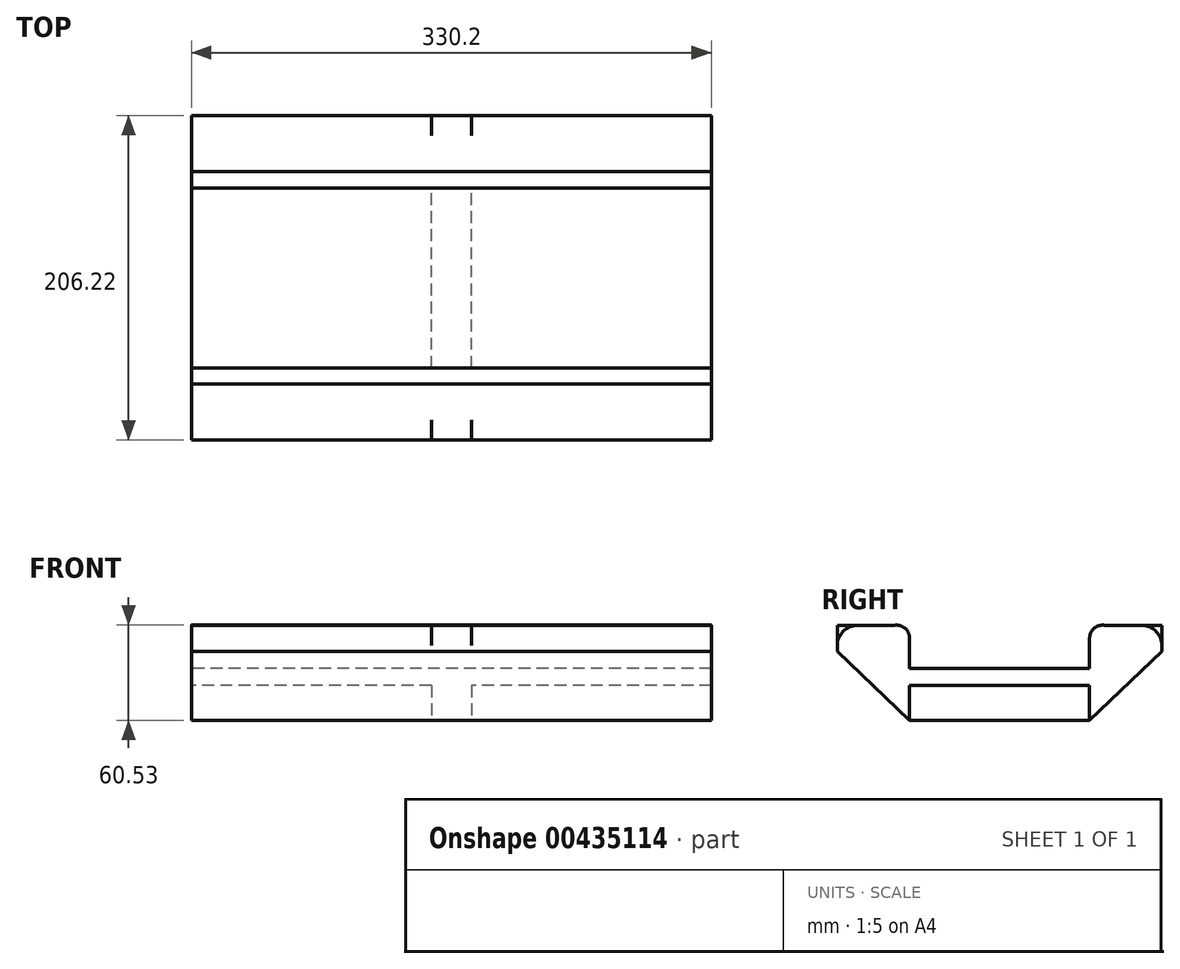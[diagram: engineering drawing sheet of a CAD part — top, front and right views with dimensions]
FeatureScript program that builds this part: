
annotation { "Feature Type Name" : "Feature", "Feature Type Description" : "" }
export const myFeature = defineFeature(function(context is Context, id is Id, definition is map)
    precondition{}
    {
        {
            var Q0;
            Q0=qCreatedBy(makeId("Right.planeOp"),FACE);
            var sketch = newSketch(context, id + "F0", { "sketchPlane" : qUnion([Q0])});
            skLineSegment(sketch, "E0.bottom", {"start": v(-57.15, 16.51) * mm, "end": v(57.15, 16.51) * mm});
            skLineSegment(sketch, "E0.top", {"start": v(-57.15, -16.51) * mm, "end": v(57.15, -16.51) * mm});
            skLineSegment(sketch, "E0.left", {"start": v(-57.15, 16.51) * mm, "end": v(-57.15, -16.51) * mm});
            skLineSegment(sketch, "E0.right", {"start": v(57.15, 16.51) * mm, "end": v(57.15, -16.51) * mm});
            skPoint(sketch, "E0.middle", {"position": v(0, 0) * mm});
            skLineSegment(sketch, "E1", {"start": v(-57.15, 16.51) * mm, "end": v(-57.15, 35.56) * mm});
            skLineSegment(sketch, "E2", {"start": v(57.15, 16.51) * mm, "end": v(57.15, 35.56) * mm});
            skLineSegment(sketch, "E3.bottom", {"start": v(-80.96, 43.82) * mm, "end": v(-103.11, 43.82) * mm});
            skLineSegment(sketch, "E3.top", {"start": v(-80.96, 27.3) * mm, "end": v(-103.11, 27.3) * mm});
            skLineSegment(sketch, "E3.left", {"start": v(-80.96, 43.82) * mm, "end": v(-80.96, 27.3) * mm});
            skLineSegment(sketch, "E3.right", {"start": v(-103.11, 43.82) * mm, "end": v(-103.11, 27.3) * mm});
            skPoint(sketch, "E3.middle", {"position": v(-92.04, 35.56) * mm});
            skLineSegment(sketch, "E4.bottom", {"start": v(103.11, 27.3) * mm, "end": v(81.47, 27.3) * mm});
            skLineSegment(sketch, "E4.top", {"start": v(103.11, 43.82) * mm, "end": v(81.47, 43.82) * mm});
            skLineSegment(sketch, "E4.left", {"start": v(103.11, 27.3) * mm, "end": v(103.11, 43.82) * mm});
            skLineSegment(sketch, "E4.right", {"start": v(81.47, 27.3) * mm, "end": v(81.47, 43.82) * mm});
            skPoint(sketch, "E4.middle", {"position": v(92.3, 35.56) * mm});
            skArc(sketch, "E5", {"start": v(-57.15, 35.56) * mm, "mid": v(-60.32, 42.16) * mm, "end": v(-67.46, 43.81) * mm});
            skArc(sketch, "E6", {"start": v(57.15, 35.56) * mm, "mid": v(60.32, 42.16) * mm, "end": v(67.46, 43.82) * mm});
            skLineSegment(sketch, "E7", {"start": v(-67.46, 43.82) * mm, "end": v(-80.96, 43.82) * mm});
            skLineSegment(sketch, "E8", {"start": v(67.46, 43.82) * mm, "end": v(81.47, 43.82) * mm});
            skLineSegment(sketch, "E9", {"start": v(-103.11, 27.3) * mm, "end": v(-57.15, -16.51) * mm});
            skLineSegment(sketch, "E10", {"start": v(103.11, 27.3) * mm, "end": v(57.15, -16.51) * mm});
            skLineSegment(sketch, "E11", {"start": v(-80.96, 27.3) * mm, "end": v(-57.15, 5.75) * mm});
            skLineSegment(sketch, "E12", {"start": v(-57.15, 5.75) * mm, "end": v(57.15, 5.75) * mm});
            skLineSegment(sketch, "E13", {"start": v(57.15, 5.75) * mm, "end": v(81.47, 27.3) * mm});
            skLineSegment(sketch, "E14", {"start": v(-65.6, 35.56) * mm, "end": v(-80.96, 27.3) * mm});
            skLineSegment(sketch, "E15", {"start": v(65.6, 35.56) * mm, "end": v(81.47, 27.3) * mm});
            skSolve(sketch);
        }
        {
            var Q0;
            {var subQ0=sQuery(id+"F0.wireOp",EDGE,"E0.bottom");Q0=makeQuery(id+"F0.imprint","IMPRINT",FACE,{"disambiguationData":[TD([[makeQuery(id+"F0.imprint","IMPRINT",EDGE,{"derivedFrom":subQ0}),-1.0]])]});}
            var Q1;
            Q1=makeQuery(id+"F0.imprint","IMPRINT",FACE,{"disambiguationData":[TD([[makeQuery(id+"F0.imprint","IMPRINT",EDGE,{"derivedFrom":sQuery(id+"F0.wireOp",EDGE,"E4.bottom")}),-1.0]])]});
            var Q2;
            Q2=makeQuery(id+"F0.imprint","IMPRINT",FACE,{"disambiguationData":[TD([[makeQuery(id+"F0.imprint","IMPRINT",EDGE,{"derivedFrom":sQuery(id+"F0.wireOp",EDGE,"E3.bottom")}),1.0]])]});
            var Q3;
            {var subQ0=sQuery(id+"F0.wireOp",EDGE,"E1");Q3=makeQuery(id+"F0.imprint","IMPRINT",FACE,{"disambiguationData":[TD([[makeQuery(id+"F0.imprint","IMPRINT",EDGE,{"derivedFrom":subQ0}),1.0]])]});}
            var Q4;
            {var subQ0=sQuery(id+"F0.wireOp",EDGE,"E2");Q4=makeQuery(id+"F0.imprint","IMPRINT",FACE,{"disambiguationData":[TD([[makeQuery(id+"F0.imprint","IMPRINT",EDGE,{"derivedFrom":subQ0}),-1.0]])]});}
            var Q5;
            Q5=makeQuery(id+"F0.imprint","IMPRINT",FACE,{"disambiguationData":[TD([[makeQuery(id+"F0.imprint","IMPRINT",EDGE,{"derivedFrom":sQuery(id+"F0.wireOp",EDGE,"E3.top")}),1.0]])]});
            var Q6;
            Q6=makeQuery(id+"F0.imprint","IMPRINT",FACE,{"disambiguationData":[TD([[makeQuery(id+"F0.imprint","IMPRINT",EDGE,{"derivedFrom":sQuery(id+"F0.wireOp",EDGE,"E4.bottom")}),1.0]])]});
            extrude(context, id + "F1", {"entities" : qUnion([Q0, Q1, Q2, Q3, Q4, Q5, Q6]), "endBound" : BoundingType.SYMMETRIC, "depth" : 304.8 * mm});
        }
        {
            var Q0;
            Q0=makeQuery(id+"F1.opExtrude","SWEPT_EDGE",EDGE,{"disambiguationData":[OSD([sQuery(id+"F0.wireOp",EDGE,"E3.bottom"),sQuery(id+"F0.wireOp",EDGE,"E3.right")])]});
            var Q1;
            Q1=makeQuery(id+"F1.opExtrude","SWEPT_EDGE",EDGE,{"disambiguationData":[OSD([sQuery(id+"F0.wireOp",EDGE,"E4.top"),sQuery(id+"F0.wireOp",EDGE,"E4.left")])]});
            fillet(context, id + "F2", {"entities" : qUnion([Q0, Q1]), "radius" : 12.7 * mm, "tangentPropagation" : true, "allowEdgeOverflow" : false});
        }
        {
            var Q0;
            Q0 = qSketchRegion(id + "F0", true);
            var Q1;
            Q1=makeQuery(id+"F1.opExtrude","CAP_FACE",FACE,{"disambiguationData":[OSD([sQuery(id+"F0.wireOp",EDGE,"E0.bottom"),sQuery(id+"F0.wireOp",EDGE,"E0.left"),sQuery(id+"F0.wireOp",EDGE,"E0.right"),sQuery(id+"F0.wireOp",EDGE,"E1"),sQuery(id+"F0.wireOp",EDGE,"E2"),sQuery(id+"F0.wireOp",EDGE,"E3.bottom"),sQuery(id+"F0.wireOp",EDGE,"E3.right"),sQuery(id+"F0.wireOp",EDGE,"E4.top"),sQuery(id+"F0.wireOp",EDGE,"E4.left"),sQuery(id+"F0.wireOp",EDGE,"E5"),sQuery(id+"F0.wireOp",EDGE,"E6"),sQuery(id+"F0.wireOp",EDGE,"E7"),sQuery(id+"F0.wireOp",EDGE,"E8"),sQuery(id+"F0.wireOp",EDGE,"E9"),sQuery(id+"F0.wireOp",EDGE,"E10"),sQuery(id+"F0.wireOp",EDGE,"E12")])],"isStart":true});
            var Q2;
            Q2=makeQuery(id+"F1.opExtrude","CAP_FACE",FACE,{"disambiguationData":[OSD([sQuery(id+"F0.wireOp",EDGE,"E0.bottom"),sQuery(id+"F0.wireOp",EDGE,"E0.left"),sQuery(id+"F0.wireOp",EDGE,"E0.right"),sQuery(id+"F0.wireOp",EDGE,"E1"),sQuery(id+"F0.wireOp",EDGE,"E2"),sQuery(id+"F0.wireOp",EDGE,"E3.bottom"),sQuery(id+"F0.wireOp",EDGE,"E3.right"),sQuery(id+"F0.wireOp",EDGE,"E4.top"),sQuery(id+"F0.wireOp",EDGE,"E4.left"),sQuery(id+"F0.wireOp",EDGE,"E5"),sQuery(id+"F0.wireOp",EDGE,"E6"),sQuery(id+"F0.wireOp",EDGE,"E7"),sQuery(id+"F0.wireOp",EDGE,"E8"),sQuery(id+"F0.wireOp",EDGE,"E9"),sQuery(id+"F0.wireOp",EDGE,"E10"),sQuery(id+"F0.wireOp",EDGE,"E12")])],"isStart":false});
            extrude(context, id + "F3", {"entities" : qUnion([Q0, Q1, Q2]), "operationType" : NewBodyOperationType.ADD, "depth" : 25.4 * mm});
        }
    });
